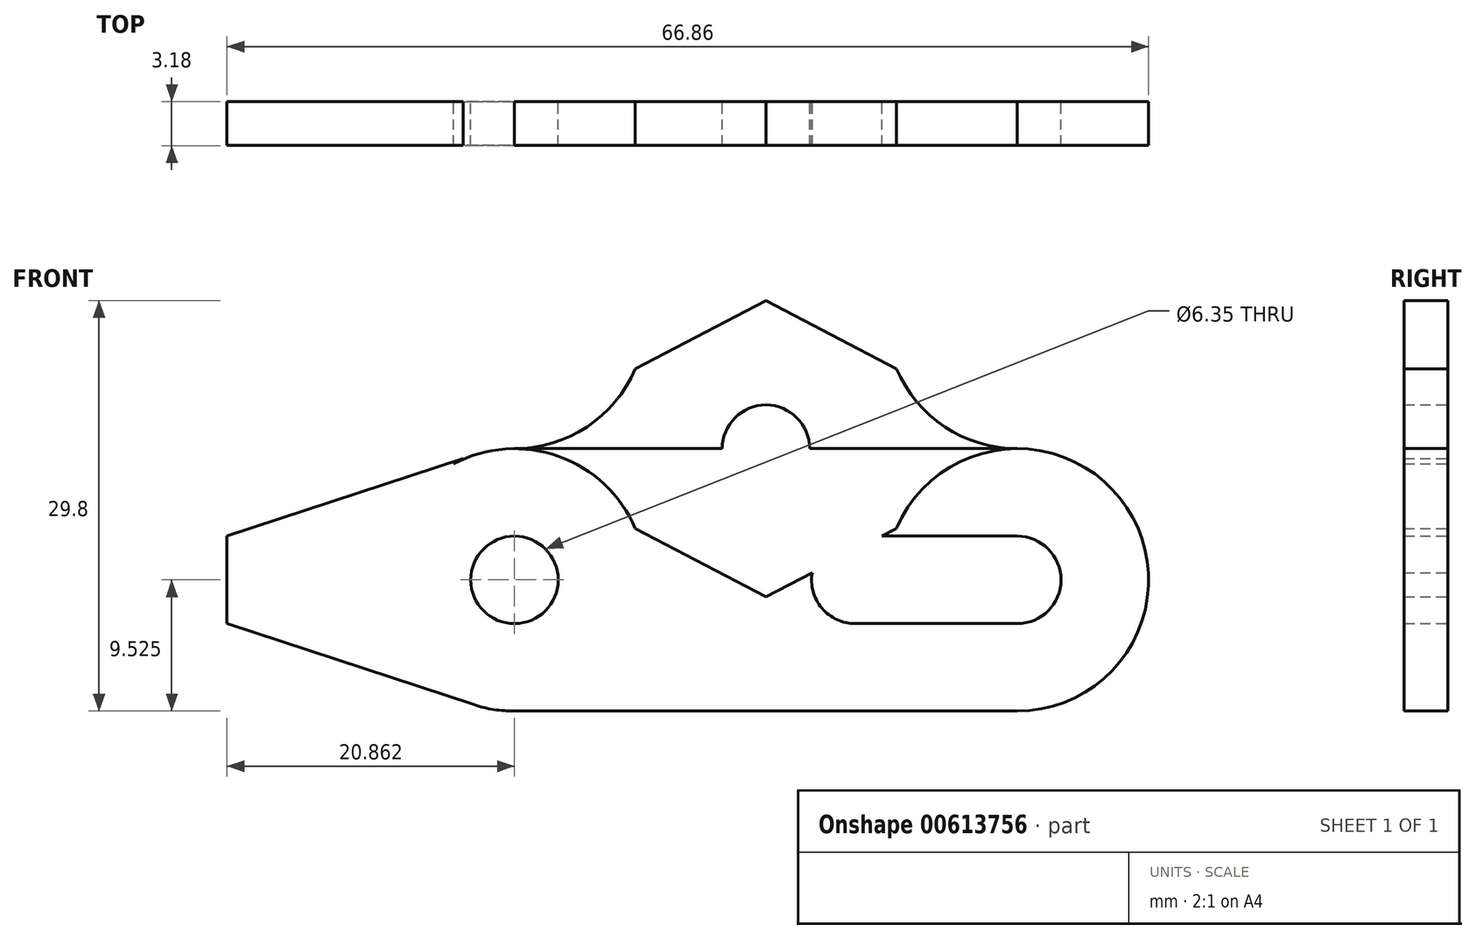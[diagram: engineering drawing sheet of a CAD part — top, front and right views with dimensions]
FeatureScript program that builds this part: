
annotation { "Feature Type Name" : "Feature", "Feature Type Description" : "" }
export const myFeature = defineFeature(function(context is Context, id is Id, definition is map)
    precondition{}
    {
        {
            var Q0;
            Q0=qCreatedBy(makeId("Front.planeOp"),FACE);
            var sketch = newSketch(context, id + "F0", { "sketchPlane" : qUnion([Q0])});
            skCircle(sketch, "E0", {"center": v(0, 0) * mm, "radius": 3.18 * mm});
            skCircle(sketch, "E1", {"center": v(18.24, 9.53) * mm, "radius": 3.18 * mm});
            skCircle(sketch, "E2", {"center": v(18.24, -9.53) * mm, "radius": 3.18 * mm});
            skCircle(sketch, "E3", {"center": v(-18.24, -9.53) * mm, "radius": 3.18 * mm});
            skCircle(sketch, "E4", {"center": v(-18.24, -9.53) * mm, "radius": 9.53 * mm});
            skCircle(sketch, "E5", {"center": v(18.24, 9.53) * mm, "radius": 9.53 * mm});
            skLineSegment(sketch, "E6", {"start": v(13.83, 17.97) * mm, "end": v(-22.65, -1.08) * mm});
            skLineSegment(sketch, "E7", {"start": v(-13.83, -17.97) * mm, "end": v(22.65, 1.08) * mm});
            skLineSegment(sketch, "E8", {"start": v(123.05, 19.05) * mm, "end": v(18.24, 19.05) * mm});
            skLineSegment(sketch, "E9.MirrorCS", {"start": v(123.05, -19.05) * mm, "end": v(18.24, -19.05) * mm});
            skCircle(sketch, "E10.MirrorC", {"center": v(18.24, -9.53) * mm, "radius": 9.53 * mm});
            skLineSegment(sketch, "E11.MirrorCS", {"start": v(13.83, -17.97) * mm, "end": v(-22.65, 1.08) * mm});
            skLineSegment(sketch, "E12.MirrorCS", {"start": v(-13.83, 17.97) * mm, "end": v(22.65, -1.08) * mm});
            skCircle(sketch, "E13.MirrorC", {"center": v(-18.24, 9.53) * mm, "radius": 9.53 * mm});
            skCircle(sketch, "E14.MirrorC", {"center": v(-18.24, 9.53) * mm, "radius": 3.18 * mm});
            skLineSegment(sketch, "E15", {"start": v(18.24, -19.05) * mm, "end": v(-18.24, -19.05) * mm});
            skLineSegment(sketch, "E16", {"start": v(-18.24, -19.05) * mm, "end": v(-51.16, -19.05) * mm});
            skLineSegment(sketch, "E17", {"start": v(-51.16, 0) * mm, "end": v(-18.24, 0) * mm});
            skLineSegment(sketch, "E18", {"start": v(-18.24, 0) * mm, "end": v(18.24, 0) * mm});
            skCircle(sketch, "E19", {"center": v(-41, 7.51) * mm, "radius": 9.53 * mm});
            skLineSegment(sketch, "E20.top", {"start": v(-41.64, 1.99) * mm, "end": v(-40.37, 1.99) * mm});
            skLineSegment(sketch, "E20.left", {"start": v(-41.64, -17.02) * mm, "end": v(-41.64, 1.99) * mm});
            skLineSegment(sketch, "E20.right", {"start": v(-40.37, -17.02) * mm, "end": v(-40.37, 1.99) * mm});
            skLineSegment(sketch, "E21", {"start": v(18.24, 0) * mm, "end": v(122.97, 0) * mm});
            skLineSegment(sketch, "E22", {"start": v(122.97, 0) * mm, "end": v(123.05, 19.05) * mm});
            skLineSegment(sketch, "E23", {"start": v(-51.16, 0) * mm, "end": v(-51.16, -19.05) * mm});
            skLineSegment(sketch, "E24.MirrorCS", {"start": v(122.97, 0) * mm, "end": v(123.05, -19.05) * mm});
            skLineSegment(sketch, "E25.right", {"start": v(-40.37, -12.7) * mm, "end": v(-40.37, -6.33) * mm});
            skLineSegment(sketch, "E26", {"start": v(-41.64, -17.02) * mm, "end": v(-40.37, -17.02) * mm});
            skLineSegment(sketch, "E27.bottom", {"start": v(-40.37, -6.33) * mm, "end": v(-39.1, -6.33) * mm});
            skLineSegment(sketch, "E27.top", {"start": v(-40.37, -12.7) * mm, "end": v(-39.1, -12.7) * mm});
            skLineSegment(sketch, "E27.left", {"start": v(-40.37, -6.33) * mm, "end": v(-40.37, -12.7) * mm});
            skLineSegment(sketch, "E28", {"start": v(-39.1, -12.7) * mm, "end": v(-21.2, -18.57) * mm});
            skLineSegment(sketch, "E29", {"start": v(-39.1, -6.33) * mm, "end": v(-39.1, -12.7) * mm});
            skLineSegment(sketch, "E30", {"start": v(-18.24, -9.53) * mm, "end": v(18.24, -9.53) * mm, "construction": true});
            skLineSegment(sketch, "E31.MirrorCS", {"start": v(-39.1, -6.35) * mm, "end": v(-21.2, -0.48) * mm});
            skCircle(sketch, "E32", {"center": v(6.5, -9.53) * mm, "radius": 3.18 * mm});
            skLineSegment(sketch, "E33", {"start": v(18.24, -12.7) * mm, "end": v(6.5, -12.7) * mm});
            skLineSegment(sketch, "E34", {"start": v(18.24, -6.35) * mm, "end": v(6.5, -6.35) * mm});
            skSolve(sketch);
        }
        {
            var Q0;
            {var subQ1=sQuery(id+"F0.wireOp",EDGE,"E28");Q0=makeQuery(id+"F0.imprint","IMPRINT",FACE,{"disambiguationData":[TD([[makeQuery(id+"F0.imprint","IMPRINT",EDGE,{"derivedFrom":subQ1}),1.0]])]});}
            var Q1;
            Q1=makeQuery(id+"F0.imprint","IMPRINT",FACE,{"disambiguationData":[TD([[makeQuery(id+"F0.imprint","IMPRINT",EDGE,{"derivedFrom":sQuery(id+"F0.wireOp",EDGE,"E3")}),-1.0]])]});
            var Q2;
            {var subQ0=sQuery(id+"F0.wireOp",EDGE,"E4");var subQ2=sQuery(id+"F0.wireOp",EDGE,"E11.MirrorCS");var subQ3=makeQuery(id+"F0.imprint","INTERSECT",VERTEX,{"disambiguationData":[OD(0.0)],"derivedFrom":[subQ0,subQ2]});Q2=makeQuery(id+"F0.imprint","IMPRINT",FACE,{"disambiguationData":[TD([[makeQuery(id+"F0.imprint","IMPRINT",EDGE,{"disambiguationData":[TD([[subQ3,-1.0]])],"derivedFrom":subQ2}),-1.0]])]});}
            var Q3;
            {var subQ5=sQuery(id+"F0.wireOp",EDGE,"E15");Q3=makeQuery(id+"F0.imprint","IMPRINT",FACE,{"disambiguationData":[TD([[makeQuery(id+"F0.imprint","IMPRINT",EDGE,{"derivedFrom":subQ5}),-1.0]])]});}
            var Q4;
            {var subQ0=sQuery(id+"F0.wireOp",EDGE,"E7");var subQ1=sQuery(id+"F0.wireOp",EDGE,"E4");var subQ2=makeQuery(id+"F0.imprint","INTERSECT",VERTEX,{"derivedFrom":[subQ1,subQ0]});Q4=makeQuery(id+"F0.imprint","IMPRINT",FACE,{"disambiguationData":[TD([[makeQuery(id+"F0.imprint","IMPRINT",EDGE,{"disambiguationData":[TD([[subQ2,-1.0]])],"derivedFrom":subQ1}),-1.0]])]});}
            var Q5;
            {var subQ0=sQuery(id+"F0.wireOp",EDGE,"E10.MirrorC");var subQ1=sQuery(id+"F0.wireOp",EDGE,"E7");var subQ2=makeQuery(id+"F0.imprint","INTERSECT",VERTEX,{"disambiguationData":[OD(0.0)],"derivedFrom":[subQ1,subQ0]});Q5=makeQuery(id+"F0.imprint","IMPRINT",FACE,{"disambiguationData":[TD([[makeQuery(id+"F0.imprint","IMPRINT",EDGE,{"disambiguationData":[TD([[subQ2,-1.0]])],"derivedFrom":subQ1}),1.0]])]});}
            var Q6;
            {var subQ0=sQuery(id+"F0.wireOp",EDGE,"E11.MirrorCS");var subQ3=sQuery(id+"F0.wireOp",EDGE,"E7");var subQ4=makeQuery(id+"F0.imprint","INTERSECT",VERTEX,{"derivedFrom":[subQ3,subQ0]});Q6=makeQuery(id+"F0.imprint","IMPRINT",FACE,{"disambiguationData":[TD([[makeQuery(id+"F0.imprint","IMPRINT",EDGE,{"disambiguationData":[TD([[subQ4,-1.0]])],"derivedFrom":subQ3}),-1.0]])]});}
            var Q7;
            {var subQ2=sQuery(id+"F0.wireOp",EDGE,"E33");var subQ4=sQuery(id+"F0.wireOp",EDGE,"E2");var subQ5=makeQuery(id+"F0.imprint","INTERSECT",VERTEX,{"derivedFrom":[subQ4,subQ2]});Q7=makeQuery(id+"F0.imprint","IMPRINT",FACE,{"disambiguationData":[TD([[makeQuery(id+"F0.imprint","IMPRINT",EDGE,{"disambiguationData":[TD([[subQ5,-1.0]])],"derivedFrom":subQ4}),-1.0]])]});}
            var Q8;
            {var subQ9=sQuery(id+"F0.wireOp",EDGE,"E18");var subQ14=sQuery(id+"F0.wireOp",EDGE,"E0");var subQ16=makeQuery(id+"F0.imprint","INTERSECT",VERTEX,{"disambiguationData":[OD(0.0)],"derivedFrom":[subQ14,subQ9]});Q8=makeQuery(id+"F0.imprint","IMPRINT",FACE,{"disambiguationData":[TD([[makeQuery(id+"F0.imprint","IMPRINT",EDGE,{"disambiguationData":[TD([[subQ16,-1.0]])],"derivedFrom":subQ14}),-1.0]])]});}
            var Q9;
            {var subQ0=sQuery(id+"F0.wireOp",EDGE,"E34");var subQ1=sQuery(id+"F0.wireOp",EDGE,"E7");var subQ2=makeQuery(id+"F0.imprint","INTERSECT",VERTEX,{"derivedFrom":[subQ1,subQ0]});Q9=makeQuery(id+"F0.imprint","IMPRINT",FACE,{"disambiguationData":[TD([[makeQuery(id+"F0.imprint","IMPRINT",EDGE,{"disambiguationData":[TD([[subQ2,-1.0]])],"derivedFrom":subQ1}),-1.0]])]});}
            extrude(context, id + "F1", {"entities" : qUnion([Q0, Q1, Q2, Q3, Q4, Q5, Q6, Q7, Q8, Q9]), "endBound" : BoundingType.SYMMETRIC, "depth" : 3.17 * mm, "offsetDistance" : 25.4 * mm});
        }
    });
